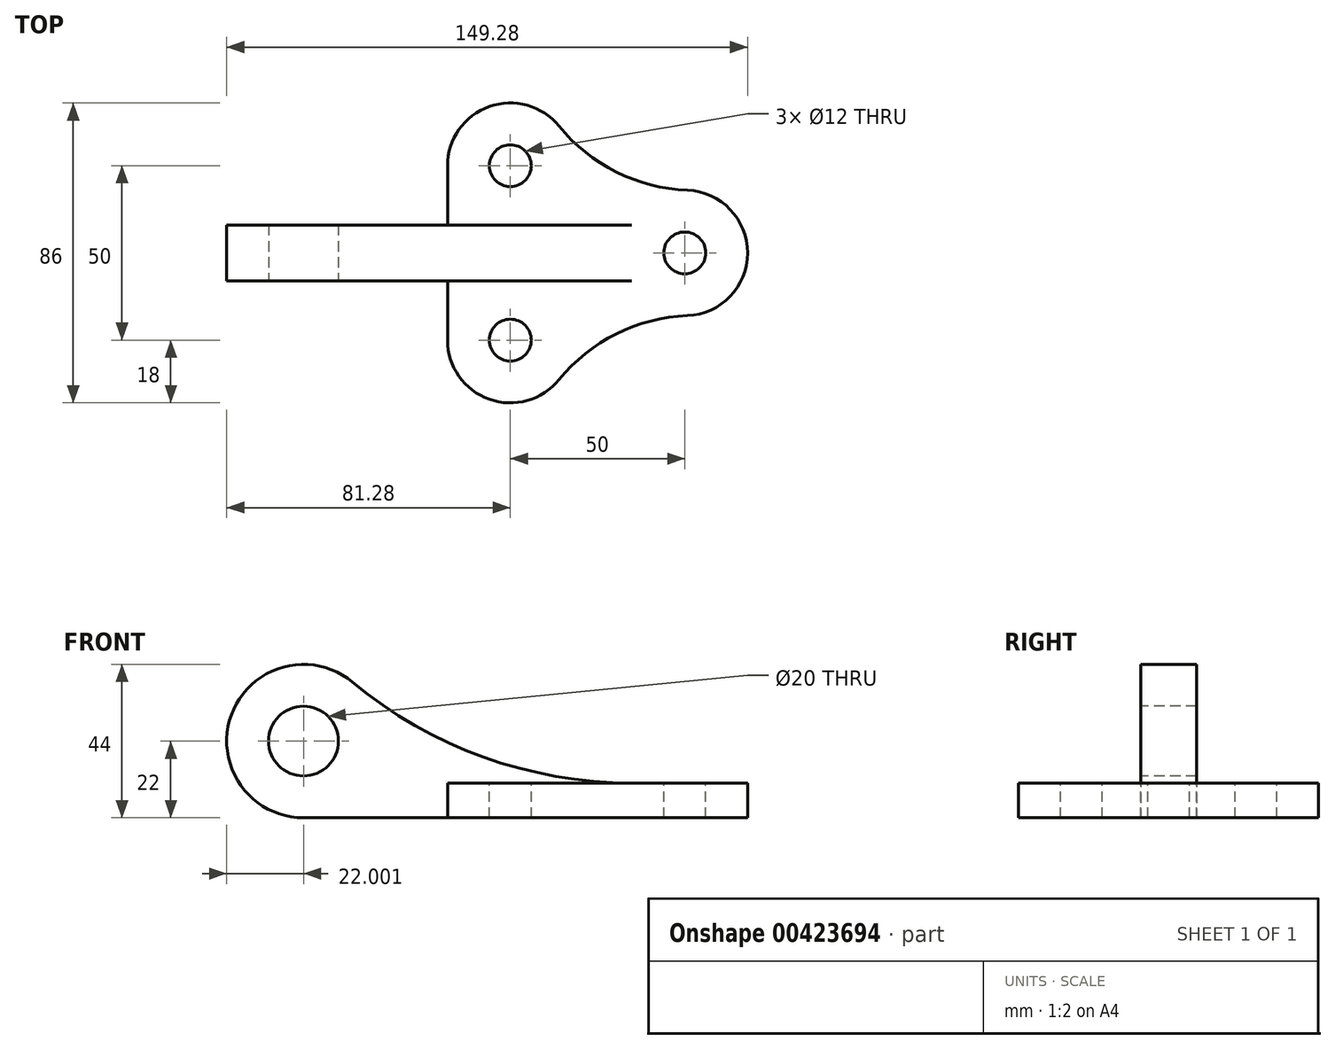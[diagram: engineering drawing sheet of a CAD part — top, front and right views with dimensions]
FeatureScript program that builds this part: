
annotation { "Feature Type Name" : "Feature", "Feature Type Description" : "" }
export const myFeature = defineFeature(function(context is Context, id is Id, definition is map)
    precondition{}
    {
        {
            var Q0;
            Q0=qCreatedBy(makeId("Top.planeOp"),FACE);
            var sketch = newSketch(context, id + "F0", { "sketchPlane" : qUnion([Q0])});
            skArc(sketch, "E0", {"start": v(50.72, -17.99) * mm, "mid": v(68, 0) * mm, "end": v(50.72, 17.99) * mm});
            skArc(sketch, "E1", {"start": v(13.96, 36.37) * mm, "mid": v(-6.03, 41.96) * mm, "end": v(-18, 25) * mm});
            skArc(sketch, "E2", {"start": v(-18, -25) * mm, "mid": v(-6.03, -41.96) * mm, "end": v(13.96, -36.37) * mm});
            skArc(sketch, "E3", {"start": v(13.96, 36.37) * mm, "mid": v(30.36, 23.22) * mm, "end": v(50.72, 17.99) * mm});
            skArc(sketch, "E4", {"start": v(50.72, -17.99) * mm, "mid": v(30.36, -23.22) * mm, "end": v(13.96, -36.37) * mm});
            skLineSegment(sketch, "E5", {"start": v(-18, 25) * mm, "end": v(-18, -25) * mm});
            skSolve(sketch);
        }
        {
            var Q0;
            Q0=makeQuery(id+"F0.imprint","IMPRINT",FACE,{"disambiguationData":[TD([[makeQuery(id+"F0.imprint","IMPRINT",EDGE,{"derivedFrom":sQuery(id+"F0.wireOp",EDGE,"E0")}),1.0]])]});
            extrude(context, id + "F1", {"entities" : qUnion([Q0]), "depth" : 10 * mm});
        }
        {
            var Q0;
            Q0=qCreatedBy(makeId("Front.planeOp"),FACE);
            var sketch = newSketch(context, id + "F2", { "sketchPlane" : qUnion([Q0])});
            skLineSegment(sketch, "E6.0", {"start": v(50.72, 10) * mm, "end": v(68, 10) * mm, "construction": true});
            skLineSegment(sketch, "E7", {"start": v(50.72, 0) * mm, "end": v(-59.28, 0) * mm});
            skArc(sketch, "E8", {"start": v(-40.84, 10) * mm, "mid": v(-69.77, 41.34) * mm, "end": v(-59.28, 0) * mm});
            skLineSegment(sketch, "E9.0", {"start": v(50.72, 10) * mm, "end": v(13.96, 10) * mm, "construction": true});
            skLineSegment(sketch, "E10", {"start": v(50.72, 10) * mm, "end": v(-40.84, 10) * mm});
            skLineSegment(sketch, "E11", {"start": v(50.72, 10) * mm, "end": v(50.72, 0) * mm});
            skSolve(sketch);
        }
        {
            var Q0;
            Q0 = qSketchRegion(id + "F2", true);
            extrude(context, id + "F3", {"entities" : qUnion([Q0]), "endBound" : BoundingType.SYMMETRIC, "depth" : 16 * mm});
        }
        {
            var Q0;
            Q0=makeQuery(id+"F3.opExtrude","SWEPT_EDGE",EDGE,{"disambiguationData":[OSD([sQuery(id+"F2.wireOp",EDGE,"E8"),sQuery(id+"F2.wireOp",EDGE,"E10")])]});
            fillet(context, id + "F4", {"entities" : qUnion([Q0]), "radius" : 125 * mm, "tangentPropagation" : true, "allowEdgeOverflow" : false});
        }
        {
            var Q0;
            Q0=makeQuery(id+"F3.opExtrude","SWEPT_BODY",BODY,{"disambiguationData":[OSD([sQuery(id+"F2.wireOp",EDGE,"E7"),sQuery(id+"F2.wireOp",EDGE,"E8"),sQuery(id+"F2.wireOp",EDGE,"E10"),sQuery(id+"F2.wireOp",EDGE,"E11")])]});
            var Q1;
            Q1=makeQuery(id+"F1.opExtrude","SWEPT_BODY",BODY,{"disambiguationData":[OSD([sQuery(id+"F0.wireOp",EDGE,"E0"),sQuery(id+"F0.wireOp",EDGE,"E1"),sQuery(id+"F0.wireOp",EDGE,"E2"),sQuery(id+"F0.wireOp",EDGE,"E3"),sQuery(id+"F0.wireOp",EDGE,"E4"),sQuery(id+"F0.wireOp",EDGE,"E5")])]});
            booleanBodies(context, id + "F5", {"operationType" : BooleanOperationType.UNION, "tools" : qUnion([Q0, Q1])});
        }
        {
            var Q0;
            Q0=makeQuery(id+"F5.opBoolean","MERGE",FACE,{"derivedFrom":[makeQuery(id+"F1.opExtrude","CAP_FACE",FACE,{"disambiguationData":[OSD([sQuery(id+"F0.wireOp",EDGE,"E0"),sQuery(id+"F0.wireOp",EDGE,"E1"),sQuery(id+"F0.wireOp",EDGE,"E2"),sQuery(id+"F0.wireOp",EDGE,"E3"),sQuery(id+"F0.wireOp",EDGE,"E4"),sQuery(id+"F0.wireOp",EDGE,"E5")])],"isStart":false}),makeQuery(id+"F3.opExtrude","SWEPT_FACE",FACE,{"disambiguationData":[OSD([sQuery(id+"F2.wireOp",EDGE,"E10")])]})]});
            var sketch = newSketch(context, id + "F6", { "sketchPlane" : qUnion([Q0])});
            skCircle(sketch, "E12", {"center": v(0, 25) * mm, "radius": 6 * mm});
            skCircle(sketch, "E13", {"center": v(0, -25) * mm, "radius": 6 * mm});
            skCircle(sketch, "E14", {"center": v(50, 0) * mm, "radius": 6 * mm});
            skSolve(sketch);
        }
        {
            var Q0;
            Q0 = qSketchRegion(id + "F6", true);
            extrude(context, id + "F7", {"entities" : qUnion([Q0]), "operationType" : NewBodyOperationType.REMOVE, "oppositeDirection" : true, "depth" : 25 * mm});
        }
        {
            var Q0;
            Q0=makeQuery(id+"F3.opExtrude","CAP_FACE",FACE,{"disambiguationData":[OSD([sQuery(id+"F2.wireOp",EDGE,"E7"),sQuery(id+"F2.wireOp",EDGE,"E8"),sQuery(id+"F2.wireOp",EDGE,"E10"),sQuery(id+"F2.wireOp",EDGE,"E11")])],"isStart":false});
            var sketch = newSketch(context, id + "F8", { "sketchPlane" : qUnion([Q0])});
            skCircle(sketch, "E15", {"center": v(-59.28, 22) * mm, "radius": 10 * mm});
            skSolve(sketch);
        }
        {
            var Q0;
            Q0 = qSketchRegion(id + "F8", true);
            extrude(context, id + "F9", {"entities" : qUnion([Q0]), "operationType" : NewBodyOperationType.REMOVE, "oppositeDirection" : true, "depth" : 25 * mm});
        }
    });
